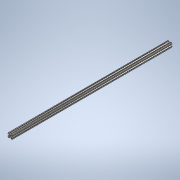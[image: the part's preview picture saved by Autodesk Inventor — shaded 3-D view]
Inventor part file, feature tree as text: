
AUTODESK INVENTOR PART (.ipt)
format: ipt  version: 2020 (Build 240168000, 168)  size: 245,760 bytes
history: native  units: in
note: dims shown in document units (in); Inventor stores cm internally (conversion verified against a paired STEP export)
features: extrude x1, sketch x1
ambient origin geometry x8: Origin, YZ Plane, XZ Plane, XY Plane, X Axis, Y Axis, Z Axis, Center Point
bodies: Solid1 (feature_tree)
feature tree (2):
  extrude  "Extrusion1"  [1 undecoded]
  sketch  "Sketch1"  dims[d0=36.0in d1=0.0in]
note: 1 required parameter value undecoded (feature->parameter linkage not recoverable at this tier; creation-order binding heuristic only, values carry confidence <= 0.55)
